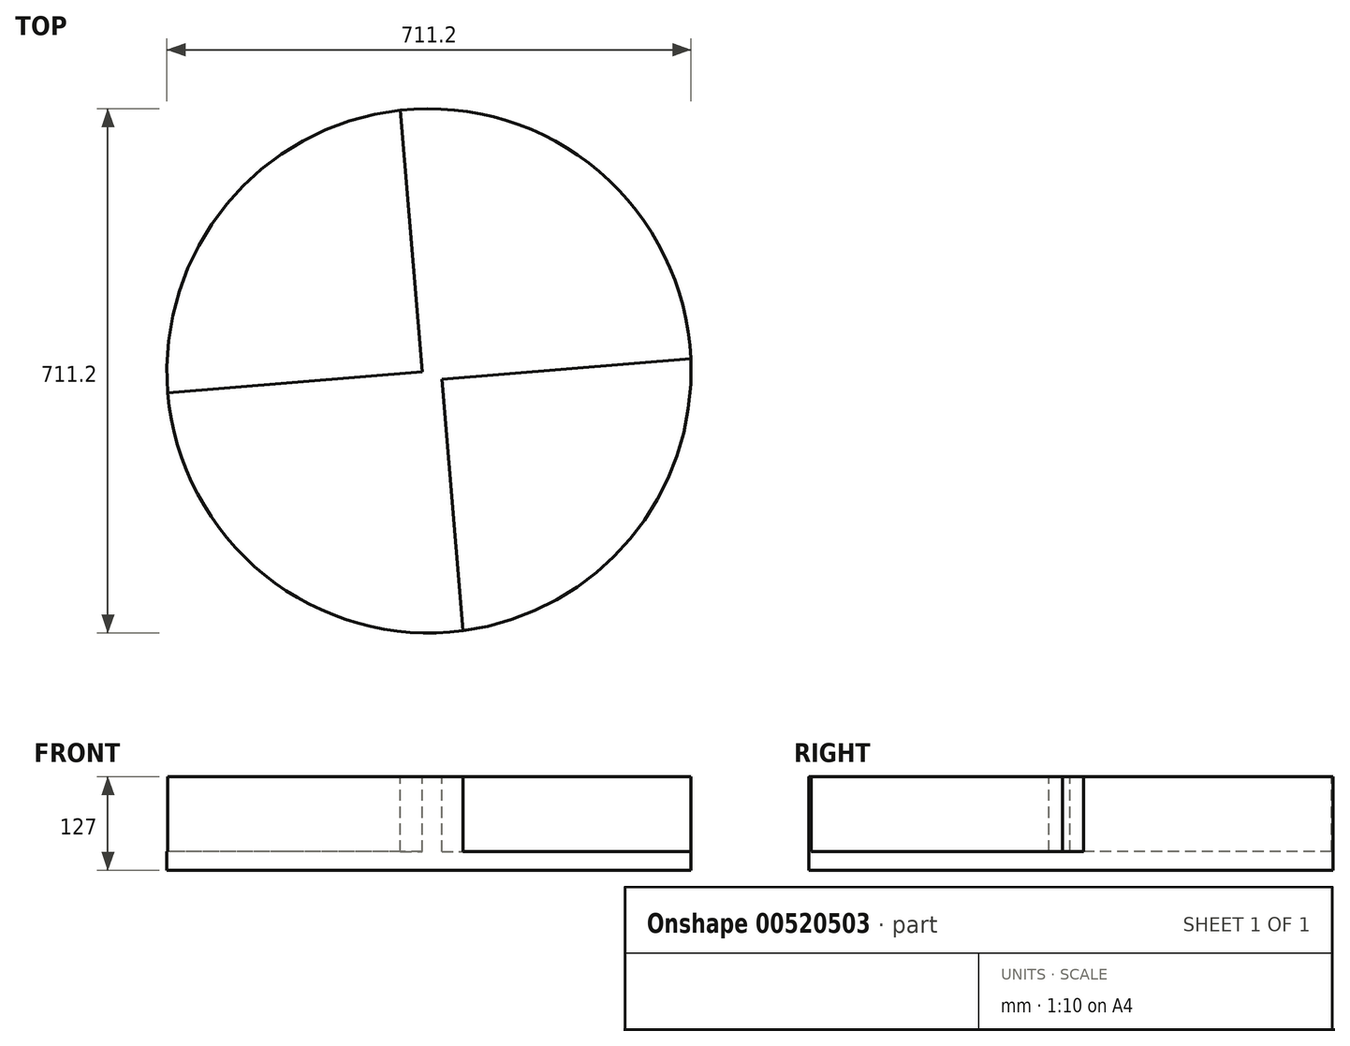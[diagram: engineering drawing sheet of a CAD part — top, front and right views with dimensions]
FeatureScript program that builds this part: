
annotation { "Feature Type Name" : "Feature", "Feature Type Description" : "" }
export const myFeature = defineFeature(function(context is Context, id is Id, definition is map)
    precondition{}
    {
        {
            var Q0;
            Q0=qCreatedBy(makeId("Top.planeOp"),FACE);
            var sketch = newSketch(context, id + "F0", { "sketchPlane" : qUnion([Q0])});
            skCircle(sketch, "E0", {"center": v(0, 0) * mm, "radius": 355.6 * mm});
            skSolve(sketch);
        }
        {
            var Q0;
            Q0=makeQuery(id+"F0.imprint","IMPRINT",FACE,{"disambiguationData":[TD([[makeQuery(id+"F0.imprint","IMPRINT",EDGE,{"derivedFrom":sQuery(id+"F0.wireOp",EDGE,"E0")}),1.0]])]});
            extrude(context, id + "F1", {"entities" : qUnion([Q0]), "depth" : 127 * mm, "offsetDistance" : 25.4 * mm});
        }
        {
            var Q0;
            Q0=makeQuery(id+"F1.opExtrude","CAP_FACE",FACE,{"disambiguationData":[OSD([sQuery(id+"F0.wireOp",EDGE,"E0")])],"isStart":false});
            var sketch = newSketch(context, id + "F2", { "sketchPlane" : qUnion([Q0])});
            skLineSegment(sketch, "E1", {"start": v(-25.94, 354.65) * mm, "end": v(33.61, -354) * mm});
            skLineSegment(sketch, "E2", {"start": v(33.61, -354) * mm, "end": v(3.86, 0) * mm});
            skLineSegment(sketch, "E3", {"start": v(3.86, 0) * mm, "end": v(354.38, 29.46) * mm});
            skLineSegment(sketch, "E4", {"start": v(354.38, 29.46) * mm, "end": v(-354.32, -30.1) * mm});
            skLineSegment(sketch, "E5", {"start": v(-13.24, 355.35) * mm, "end": v(46.37, -354) * mm});
            skLineSegment(sketch, "E6", {"start": v(-38.64, 353.5) * mm, "end": v(20.81, -354) * mm});
            skLineSegment(sketch, "E7", {"start": v(353.1, 42.1) * mm, "end": v(-354.32, -17.36) * mm});
            skLineSegment(sketch, "E8", {"start": v(-353.02, -42.76) * mm, "end": v(355.2, 16.76) * mm});
            skSolve(sketch);
        }
        {
            var Q0;
            {var subQ0=sQuery(id+"F2.wireOp",EDGE,"E4");var subQ1=makeQuery(id+"F1.opExtrude","CAP_EDGE",EDGE,{"disambiguationData":[OSD([sQuery(id+"F0.wireOp",EDGE,"E0")])],"isStart":false});var subQ2=makeQuery(id+"F2.imprint","INTERSECT",VERTEX,{"disambiguationData":[OD(1.0)],"derivedFrom":[subQ1,subQ0]});Q0=makeQuery(id+"F2.imprint","IMPRINT",FACE,{"disambiguationData":[TD([[makeQuery(id+"F2.imprint","IMPRINT",EDGE,{"disambiguationData":[TD([[subQ2,1.0]])],"derivedFrom":subQ0}),-1.0]])]});}
            var Q1;
            {var subQ0=sQuery(id+"F2.wireOp",EDGE,"E5");var subQ1=makeQuery(id+"F1.opExtrude","CAP_EDGE",EDGE,{"disambiguationData":[OSD([sQuery(id+"F0.wireOp",EDGE,"E0")])],"isStart":false});var subQ2=makeQuery(id+"F2.imprint","INTERSECT",VERTEX,{"disambiguationData":[OD(0.0)],"derivedFrom":[subQ1,subQ0]});Q1=makeQuery(id+"F2.imprint","IMPRINT",FACE,{"disambiguationData":[TD([[makeQuery(id+"F2.imprint","IMPRINT",EDGE,{"disambiguationData":[TD([[subQ2,-1.0]])],"derivedFrom":subQ0}),1.0]])]});}
            var Q2;
            {var subQ0=sQuery(id+"F2.wireOp",EDGE,"E2");var subQ1=makeQuery(id+"F1.opExtrude","CAP_EDGE",EDGE,{"disambiguationData":[OSD([sQuery(id+"F0.wireOp",EDGE,"E0")])],"isStart":false});var subQ2=makeQuery(id+"F2.imprint","INTERSECT",VERTEX,{"derivedFrom":[subQ1,subQ0]});Q2=makeQuery(id+"F2.imprint","IMPRINT",FACE,{"disambiguationData":[TD([[makeQuery(id+"F2.imprint","IMPRINT",EDGE,{"disambiguationData":[TD([[subQ2,-1.0]])],"derivedFrom":subQ0}),1.0]])]});}
            var Q3;
            {var subQ0=sQuery(id+"F2.wireOp",EDGE,"E8");var subQ1=sQuery(id+"F2.wireOp",EDGE,"E5");var subQ2=makeQuery(id+"F2.imprint","INTERSECT",VERTEX,{"derivedFrom":[subQ1,subQ0]});Q3=makeQuery(id+"F2.imprint","IMPRINT",FACE,{"disambiguationData":[TD([[makeQuery(id+"F2.imprint","IMPRINT",EDGE,{"disambiguationData":[TD([[subQ2,-1.0]])],"derivedFrom":subQ1}),1.0]])]});}
            extrude(context, id + "F3", {"entities" : qUnion([Q0, Q1, Q2, Q3]), "operationType" : NewBodyOperationType.REMOVE, "oppositeDirection" : true, "depth" : 101.6 * mm, "offsetDistance" : 25.4 * mm});
        }
    });
